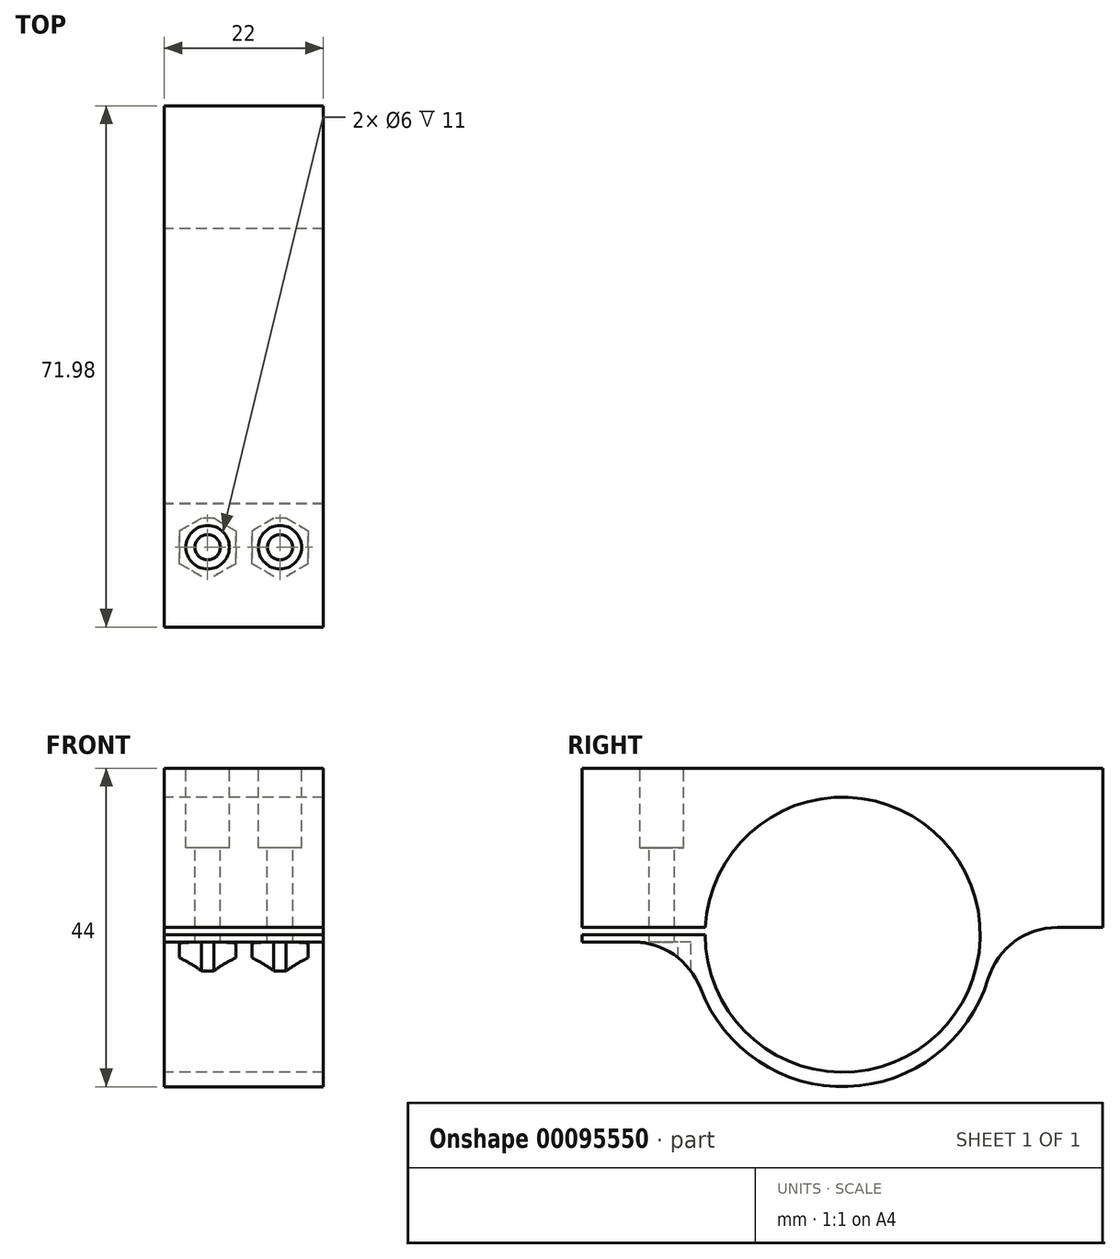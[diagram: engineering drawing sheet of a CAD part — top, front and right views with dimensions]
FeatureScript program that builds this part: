
annotation { "Feature Type Name" : "Feature", "Feature Type Description" : "" }
export const myFeature = defineFeature(function(context is Context, id is Id, definition is map)
    precondition{}
    {
        {
            var Q0;
            Q0=qCreatedBy(makeId("Right.planeOp"),FACE);
            var sketch = newSketch(context, id + "F0", { "sketchPlane" : qUnion([Q0])});
            skArc(sketch, "E0", {"start": v(-19, 0) * mm, "mid": v(19, -0.5) * mm, "end": v(-18.97, 1) * mm});
            skArc(sketch, "E1", {"start": v(-21, 0) * mm, "mid": v(21, -0.5) * mm, "end": v(-20.98, 1) * mm});
            skLineSegment(sketch, "E2", {"start": v(0, 0) * mm, "end": v(-21, 0) * mm});
            skLineSegment(sketch, "E3", {"start": v(-21, 0) * mm, "end": v(-36, 0) * mm});
            skLineSegment(sketch, "E4.bottom", {"start": v(0, 0) * mm, "end": v(-36, 0) * mm});
            skLineSegment(sketch, "E4.top", {"start": v(0, 1) * mm, "end": v(-36, 1) * mm});
            skLineSegment(sketch, "E4.left", {"start": v(0, 0) * mm, "end": v(0, 1) * mm});
            skLineSegment(sketch, "E4.right", {"start": v(-36, 0) * mm, "end": v(-36, 1) * mm});
            skPoint(sketch, "E5", {"position": v(-20.98, 1) * mm});
            skPoint(sketch, "E6", {"position": v(-18.97, 1) * mm});
            skLineSegment(sketch, "E7.bottom", {"start": v(-36, 1) * mm, "end": v(35.98, 1) * mm});
            skLineSegment(sketch, "E7.top", {"start": v(-36, 23) * mm, "end": v(35.98, 23) * mm});
            skLineSegment(sketch, "E7.left", {"start": v(-36, 1) * mm, "end": v(-36, 23) * mm});
            skLineSegment(sketch, "E7.right", {"start": v(35.98, 1) * mm, "end": v(35.98, 23) * mm});
            skPoint(sketch, "E8", {"position": v(20.98, 1) * mm});
            skLineSegment(sketch, "E9", {"start": v(20.98, 1) * mm, "end": v(35.98, 1) * mm});
            skLineSegment(sketch, "E10.bottom", {"start": v(-36, 0) * mm, "end": v(-18.97, 0) * mm});
            skLineSegment(sketch, "E10.top", {"start": v(-36, -1) * mm, "end": v(-18.97, -1) * mm});
            skLineSegment(sketch, "E10.left", {"start": v(-36, 0) * mm, "end": v(-36, -1) * mm});
            skLineSegment(sketch, "E10.right", {"start": v(-18.97, 0) * mm, "end": v(-18.97, -1) * mm});
            skSolve(sketch);
        }
        {
            var Q0;
            Q0=makeQuery(id+"F0.imprint","IMPRINT",FACE,{"disambiguationData":[TD([[makeQuery(id+"F0.imprint","IMPRINT",EDGE,{"derivedFrom":sQuery(id+"F0.wireOp",EDGE,"E7.top")}),-1.0]])]});
            var Q1;
            {var subQ0=sQuery(id+"F0.wireOp",EDGE,"E4.bottom");var subQ1=sQuery(id+"F0.wireOp",EDGE,"E0");var subQ2=makeQuery(id+"F0.imprint","INTERSECT",VERTEX,{"derivedFrom":[subQ1,subQ0]});Q1=makeQuery(id+"F0.imprint","IMPRINT",FACE,{"disambiguationData":[TD([[makeQuery(id+"F0.imprint","IMPRINT",EDGE,{"disambiguationData":[TD([[subQ2,-1.0]])],"derivedFrom":subQ1}),-1.0]])]});}
            var Q2;
            {var subQ0=sQuery(id+"F0.wireOp",EDGE,"E7.bottom");var subQ1=sQuery(id+"F0.wireOp",EDGE,"E0");var subQ2=makeQuery(id+"F0.imprint","INTERSECT",VERTEX,{"disambiguationData":[OD(0.0)],"derivedFrom":[subQ1,subQ0]});Q2=makeQuery(id+"F0.imprint","IMPRINT",FACE,{"disambiguationData":[TD([[makeQuery(id+"F0.imprint","IMPRINT",EDGE,{"disambiguationData":[TD([[subQ2,1.0]])],"derivedFrom":subQ1}),-1.0]])]});}
            var Q3;
            {var subQ1=sQuery(id+"F0.wireOp",EDGE,"E0");var subQ3=sQuery(id+"F0.wireOp",EDGE,"E7.bottom");var subQ4=makeQuery(id+"F0.imprint","INTERSECT",VERTEX,{"disambiguationData":[OD(1.0)],"derivedFrom":[subQ1,subQ3]});Q3=makeQuery(id+"F0.imprint","IMPRINT",FACE,{"disambiguationData":[TD([[makeQuery(id+"F0.imprint","IMPRINT",EDGE,{"disambiguationData":[TD([[subQ4,1.0]])],"derivedFrom":subQ1}),-1.0]])]});}
            var Q4;
            {var subQ5=sQuery(id+"F0.wireOp",EDGE,"E10.left");Q4=makeQuery(id+"F0.imprint","IMPRINT",FACE,{"disambiguationData":[TD([[makeQuery(id+"F0.imprint","IMPRINT",EDGE,{"derivedFrom":subQ5}),1.0]])]});}
            extrude(context, id + "F1", {"entities" : qUnion([Q0, Q1, Q2, Q3, Q4]), "depth" : 22 * mm});
        }
        {
            var Q0;
            Q0=makeQuery(id+"F1.opExtrude","SWEPT_FACE",FACE,{"disambiguationData":[OSD([sQuery(id+"F0.wireOp",EDGE,"E7.top")])]});
            var sketch = newSketch(context, id + "F2", { "sketchPlane" : qUnion([Q0])});
            skCircle(sketch, "E11", {"center": v(6, -24.98) * mm, "radius": 1.75 * mm});
            skPoint(sketch, "E12.top.end.orphan", {"position": v(11, -36) * mm});
            skLineSegment(sketch, "E13", {"start": v(6, -24.98) * mm, "end": v(0, -24.98) * mm});
            skLineSegment(sketch, "E14", {"start": v(0, 0) * mm, "end": v(5, 0) * mm});
            skLineSegment(sketch, "E15", {"start": v(6, -24.98) * mm, "end": v(5, 0) * mm});
            skLineSegment(sketch, "E16", {"start": v(6, -24.98) * mm, "end": v(16, -24.98) * mm});
            skCircle(sketch, "E17", {"center": v(16, -24.98) * mm, "radius": 1.75 * mm});
            skCircle(sketch, "E18", {"center": v(16, -24.98) * mm, "radius": 3 * mm});
            skCircle(sketch, "E19", {"center": v(6, -24.98) * mm, "radius": 3 * mm});
            skCircle(sketch, "E20.cCircle", {"center": v(16, -24.98) * mm, "radius": 4.5 * mm, "construction": true});
            skLineSegment(sketch, "E20.0", {"start": v(16, -20.48) * mm, "end": v(19.9, -22.73) * mm});
            skLineSegment(sketch, "E20.1", {"start": v(19.9, -22.73) * mm, "end": v(19.9, -27.23) * mm});
            skLineSegment(sketch, "E20.2", {"start": v(19.9, -27.23) * mm, "end": v(16, -29.48) * mm});
            skLineSegment(sketch, "E20.3", {"start": v(16, -29.48) * mm, "end": v(12.1, -27.23) * mm});
            skLineSegment(sketch, "E20.4", {"start": v(12.1, -27.23) * mm, "end": v(12.1, -22.73) * mm});
            skLineSegment(sketch, "E20.5", {"start": v(12.1, -22.73) * mm, "end": v(16, -20.48) * mm});
            skCircle(sketch, "E21.cCircle", {"center": v(6, -24.98) * mm, "radius": 4.5 * mm, "construction": true});
            skLineSegment(sketch, "E21.0", {"start": v(5.82, -20.48) * mm, "end": v(9.8, -22.58) * mm});
            skLineSegment(sketch, "E21.1", {"start": v(9.8, -22.58) * mm, "end": v(9.98, -27.07) * mm});
            skLineSegment(sketch, "E21.2", {"start": v(9.98, -27.07) * mm, "end": v(6.18, -29.48) * mm});
            skLineSegment(sketch, "E21.3", {"start": v(6.18, -29.48) * mm, "end": v(2.2, -27.38) * mm});
            skLineSegment(sketch, "E21.4", {"start": v(2.2, -27.38) * mm, "end": v(2.02, -22.89) * mm});
            skLineSegment(sketch, "E21.5", {"start": v(2.02, -22.89) * mm, "end": v(5.82, -20.48) * mm});
            skSolve(sketch);
        }
        {
            var Q0;
            {var subQ0=sQuery(id+"F2.wireOp",EDGE,"E13");var subQ1=sQuery(id+"F2.wireOp",EDGE,"E11");var subQ2=makeQuery(id+"F2.imprint","INTERSECT",VERTEX,{"derivedFrom":[subQ1,subQ0]});Q0=makeQuery(id+"F2.imprint","IMPRINT",FACE,{"disambiguationData":[TD([[makeQuery(id+"F2.imprint","IMPRINT",EDGE,{"disambiguationData":[TD([[subQ2,-1.0]])],"derivedFrom":subQ1}),1.0]])]});}
            var Q1;
            {var subQ0=sQuery(id+"F2.wireOp",EDGE,"E13");var subQ1=sQuery(id+"F2.wireOp",EDGE,"E11");var subQ2=makeQuery(id+"F2.imprint","INTERSECT",VERTEX,{"derivedFrom":[subQ1,subQ0]});Q1=makeQuery(id+"F2.imprint","IMPRINT",FACE,{"disambiguationData":[TD([[makeQuery(id+"F2.imprint","IMPRINT",EDGE,{"disambiguationData":[TD([[subQ2,1.0]])],"derivedFrom":subQ1}),1.0]])]});}
            var Q2;
            {var subQ0=sQuery(id+"F2.wireOp",EDGE,"E16");var subQ1=sQuery(id+"F2.wireOp",EDGE,"E11");var subQ2=makeQuery(id+"F2.imprint","INTERSECT",VERTEX,{"derivedFrom":[subQ1,subQ0]});Q2=makeQuery(id+"F2.imprint","IMPRINT",FACE,{"disambiguationData":[TD([[makeQuery(id+"F2.imprint","IMPRINT",EDGE,{"disambiguationData":[TD([[subQ2,-1.0]])],"derivedFrom":subQ1}),1.0]])]});}
            var Q3;
            Q3=makeQuery(id+"F2.imprint","IMPRINT",FACE,{"disambiguationData":[TD([[makeQuery(id+"F2.imprint","IMPRINT",EDGE,{"derivedFrom":sQuery(id+"F2.wireOp",EDGE,"E17")}),1.0]])]});
            extrude(context, id + "F3", {"entities" : qUnion([Q0, Q1, Q2, Q3]), "operationType" : NewBodyOperationType.REMOVE, "oppositeDirection" : true, "depth" : 25 * mm});
        }
        {
            var Q0;
            {var subQ0=sQuery(id+"F2.wireOp",EDGE,"E16");var subQ1=sQuery(id+"F2.wireOp",EDGE,"E11");var subQ2=makeQuery(id+"F2.imprint","INTERSECT",VERTEX,{"derivedFrom":[subQ1,subQ0]});Q0=makeQuery(id+"F2.imprint","IMPRINT",FACE,{"disambiguationData":[TD([[makeQuery(id+"F2.imprint","IMPRINT",EDGE,{"disambiguationData":[TD([[subQ2,1.0]])],"derivedFrom":subQ1}),-1.0]])]});}
            var Q1;
            {var subQ0=sQuery(id+"F2.wireOp",EDGE,"E15");var subQ1=sQuery(id+"F2.wireOp",EDGE,"E11");var subQ2=makeQuery(id+"F2.imprint","INTERSECT",VERTEX,{"derivedFrom":[subQ1,subQ0]});Q1=makeQuery(id+"F2.imprint","IMPRINT",FACE,{"disambiguationData":[TD([[makeQuery(id+"F2.imprint","IMPRINT",EDGE,{"disambiguationData":[TD([[subQ2,-1.0]])],"derivedFrom":subQ1}),-1.0]])]});}
            var Q2;
            {var subQ0=sQuery(id+"F2.wireOp",EDGE,"E15");var subQ1=sQuery(id+"F2.wireOp",EDGE,"E11");var subQ2=makeQuery(id+"F2.imprint","INTERSECT",VERTEX,{"derivedFrom":[subQ1,subQ0]});Q2=makeQuery(id+"F2.imprint","IMPRINT",FACE,{"disambiguationData":[TD([[makeQuery(id+"F2.imprint","IMPRINT",EDGE,{"disambiguationData":[TD([[subQ2,1.0]])],"derivedFrom":subQ1}),-1.0]])]});}
            var Q3;
            Q3=makeQuery(id+"F2.imprint","IMPRINT",FACE,{"disambiguationData":[TD([[makeQuery(id+"F2.imprint","IMPRINT",EDGE,{"derivedFrom":sQuery(id+"F2.wireOp",EDGE,"E17")}),-1.0]])]});
            extrude(context, id + "F4", {"entities" : qUnion([Q0, Q1, Q2, Q3]), "operationType" : NewBodyOperationType.REMOVE, "oppositeDirection" : true, "depth" : 11 * mm});
        }
        {
            var Q0;
            Q0=makeQuery(id+"F1.opExtrude","SWEPT_FACE",FACE,{"disambiguationData":[OSD([sQuery(id+"F0.wireOp",EDGE,"E10.top")])]});
            var sketch = newSketch(context, id + "F5", { "sketchPlane" : qUnion([Q0])});
            skCircle(sketch, "E22.cCircle", {"center": v(16, 24.98) * mm, "radius": 4.5 * mm, "construction": true});
            skLineSegment(sketch, "E22.0", {"start": v(16, 29.48) * mm, "end": v(19.9, 27.23) * mm});
            skLineSegment(sketch, "E22.1", {"start": v(19.9, 27.23) * mm, "end": v(19.9, 22.73) * mm});
            skLineSegment(sketch, "E22.2", {"start": v(19.9, 22.73) * mm, "end": v(16, 20.48) * mm});
            skLineSegment(sketch, "E22.3", {"start": v(16, 20.48) * mm, "end": v(12.1, 22.73) * mm});
            skLineSegment(sketch, "E22.4", {"start": v(12.1, 22.73) * mm, "end": v(12.1, 27.23) * mm});
            skLineSegment(sketch, "E22.5", {"start": v(12.1, 27.23) * mm, "end": v(16, 29.48) * mm});
            skCircle(sketch, "E23.cCircle", {"center": v(6, 24.98) * mm, "radius": 4.5 * mm, "construction": true});
            skLineSegment(sketch, "E23.0", {"start": v(6, 29.48) * mm, "end": v(9.9, 27.23) * mm});
            skLineSegment(sketch, "E23.1", {"start": v(9.9, 27.23) * mm, "end": v(9.9, 22.73) * mm});
            skLineSegment(sketch, "E23.2", {"start": v(9.9, 22.73) * mm, "end": v(6, 20.48) * mm});
            skLineSegment(sketch, "E23.3", {"start": v(6, 20.48) * mm, "end": v(2.1, 22.73) * mm});
            skLineSegment(sketch, "E23.4", {"start": v(2.1, 22.73) * mm, "end": v(2.1, 27.23) * mm});
            skLineSegment(sketch, "E23.5", {"start": v(2.1, 27.23) * mm, "end": v(6, 29.48) * mm});
            skSolve(sketch);
        }
        {
            var Q0;
            Q0=makeQuery(id+"F5.imprint","IMPRINT",FACE,{"disambiguationData":[TD([[makeQuery(id+"F5.imprint","IMPRINT",EDGE,{"derivedFrom":sQuery(id+"F5.wireOp",EDGE,"E22.0")}),-1.0]])]});
            var Q1;
            Q1=makeQuery(id+"F5.imprint","IMPRINT",FACE,{"disambiguationData":[TD([[makeQuery(id+"F5.imprint","IMPRINT",EDGE,{"derivedFrom":sQuery(id+"F5.wireOp",EDGE,"E23.0")}),-1.0]])]});
            extrude(context, id + "F6", {"entities" : qUnion([Q0, Q1]), "depth" : 20 * mm});
        }
        {
            var Q0;
            Q0=makeQuery(id+"F1.opExtrude","SWEPT_EDGE",EDGE,{"disambiguationData":[OSD([sQuery(id+"F0.wireOp",EDGE,"E1"),sQuery(id+"F0.wireOp",EDGE,"E7.bottom"),sQuery(id+"F0.wireOp",EDGE,"E9")])]});
            var Q1;
            Q1=makeQuery(id+"F1.opExtrude","SWEPT_EDGE",EDGE,{"disambiguationData":[OSD([sQuery(id+"F0.wireOp",EDGE,"E1"),sQuery(id+"F0.wireOp",EDGE,"E10.top")])]});
            fillet(context, id + "F7", {"entities" : qUnion([Q0, Q1]), "radius" : 10 * mm, "tangentPropagation" : true, "allowEdgeOverflow" : false});
        }
        {
            var Q0;
            Q0=makeQuery(id+"F6.opExtrude","SWEPT_BODY",BODY,{"disambiguationData":[OSD([sQuery(id+"F0.wireOp",EDGE,"E10.top"),sQuery(id+"F2.wireOp",EDGE,"E17"),sQuery(id+"F5.wireOp",EDGE,"E22.0"),sQuery(id+"F5.wireOp",EDGE,"E22.1"),sQuery(id+"F5.wireOp",EDGE,"E22.2"),sQuery(id+"F5.wireOp",EDGE,"E22.3"),sQuery(id+"F5.wireOp",EDGE,"E22.4"),sQuery(id+"F5.wireOp",EDGE,"E22.5")])]});
            var Q1;
            Q1=makeQuery(id+"F6.opExtrude","SWEPT_BODY",BODY,{"disambiguationData":[OSD([sQuery(id+"F0.wireOp",EDGE,"E10.top"),sQuery(id+"F2.wireOp",EDGE,"E11"),sQuery(id+"F5.wireOp",EDGE,"E23.0"),sQuery(id+"F5.wireOp",EDGE,"E23.1"),sQuery(id+"F5.wireOp",EDGE,"E23.2"),sQuery(id+"F5.wireOp",EDGE,"E23.3"),sQuery(id+"F5.wireOp",EDGE,"E23.4"),sQuery(id+"F5.wireOp",EDGE,"E23.5")])]});
            var Q2;
            Q2=makeQuery(id+"F1.opExtrude","SWEPT_BODY",BODY,{"disambiguationData":[OSD([sQuery(id+"F0.wireOp",EDGE,"E0"),sQuery(id+"F0.wireOp",EDGE,"E1"),sQuery(id+"F0.wireOp",EDGE,"E7.bottom"),sQuery(id+"F0.wireOp",EDGE,"E7.top"),sQuery(id+"F0.wireOp",EDGE,"E7.left"),sQuery(id+"F0.wireOp",EDGE,"E7.right"),sQuery(id+"F0.wireOp",EDGE,"E9"),sQuery(id+"F0.wireOp",EDGE,"E10.bottom"),sQuery(id+"F0.wireOp",EDGE,"E10.top"),sQuery(id+"F0.wireOp",EDGE,"E10.left")])]});
            booleanBodies(context, id + "F8", {"operationType" : BooleanOperationType.SUBTRACTION, "tools" : qUnion([Q0, Q1]), "targets" : qUnion([Q2])});
        }
    });
